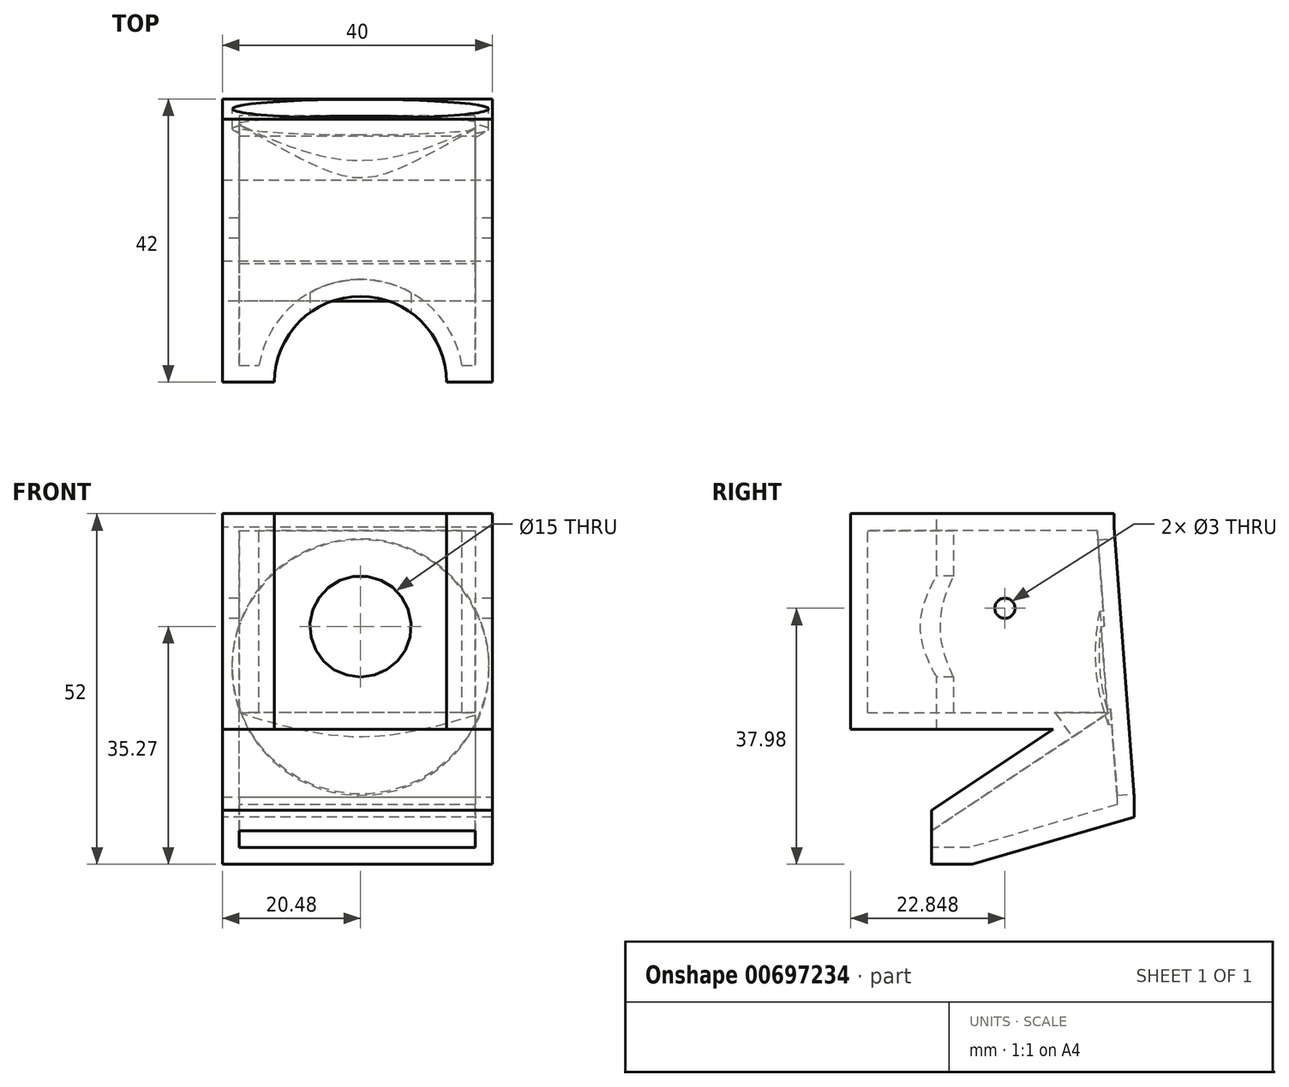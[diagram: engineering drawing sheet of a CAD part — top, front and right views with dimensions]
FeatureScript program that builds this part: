
annotation { "Feature Type Name" : "Feature", "Feature Type Description" : "" }
export const myFeature = defineFeature(function(context is Context, id is Id, definition is map)
    precondition{}
    {
        {
            var Q0;
            Q0=qCreatedBy(makeId("Top.planeOp"),FACE);
            var sketch = newSketch(context, id + "F0", { "sketchPlane" : qUnion([Q0])});
            skLineSegment(sketch, "E0.bottom", {"start": v(-20.48, 30.45) * mm, "end": v(19.52, 30.45) * mm});
            skLineSegment(sketch, "E0.top", {"start": v(-20.48, 0.45) * mm, "end": v(19.52, 0.45) * mm});
            skLineSegment(sketch, "E0.left", {"start": v(-20.48, 30.45) * mm, "end": v(-20.48, 0.45) * mm});
            skLineSegment(sketch, "E0.right", {"start": v(19.52, 30.45) * mm, "end": v(19.52, 0.45) * mm});
            skSolve(sketch);
        }
        {
            var Q0;
            Q0=makeQuery(id+"F0.imprint","IMPRINT",FACE,{"disambiguationData":[TD([[makeQuery(id+"F0.imprint","IMPRINT",EDGE,{"derivedFrom":sQuery(id+"F0.wireOp",EDGE,"E0.bottom")}),-1.0]])]});
            extrude(context, id + "F1", {"entities" : qUnion([Q0]), "depth" : 20 * mm, "offsetDistance" : 25 * mm});
        }
        {
            var Q0;
            Q0=makeQuery(id+"F1.opExtrude","CAP_EDGE",EDGE,{"disambiguationData":[OSD([sQuery(id+"F0.wireOp",EDGE,"E0.top")])],"isStart":false});
            chamfer(context, id + "F2", {"entities" : qUnion([Q0]), "chamferType" : ChamferType.TWO_OFFSETS, "width1" : 18 * mm, "oppositeDirection" : false, "width2" : 12 * mm, "tangentPropagation" : true});
        }
        {
            var Q0;
            Q0=makeQuery(id+"F1.opExtrude","CAP_EDGE",EDGE,{"disambiguationData":[OSD([sQuery(id+"F0.wireOp",EDGE,"E0.bottom")])],"isStart":true});
            chamfer(context, id + "F3", {"entities" : qUnion([Q0]), "chamferType" : ChamferType.TWO_OFFSETS, "width1" : 24 * mm, "oppositeDirection" : false, "width2" : 7 * mm, "tangentPropagation" : true});
        }
        {
            var Q0;
            Q0=makeQuery(id+"F1.opExtrude","CAP_FACE",FACE,{"disambiguationData":[OSD([sQuery(id+"F0.wireOp",EDGE,"E0.bottom"),sQuery(id+"F0.wireOp",EDGE,"E0.top"),sQuery(id+"F0.wireOp",EDGE,"E0.left"),sQuery(id+"F0.wireOp",EDGE,"E0.right")])],"isStart":false});
            extrude(context, id + "F4", {"entities" : qUnion([Q0]), "operationType" : NewBodyOperationType.ADD, "depth" : 30 * mm, "offsetDistance" : 25 * mm});
        }
        {
            var Q0;
            Q0=makeQuery(id+"F4.opExtrude","CAP_EDGE",EDGE,{"disambiguationData":[OSD([sQuery(id+"F0.wireOp",EDGE,"E0.bottom")])],"isStart":false});
            chamfer(context, id + "F5", {"entities" : qUnion([Q0]), "chamferType" : ChamferType.TWO_OFFSETS, "width1" : 40 * mm, "oppositeDirection" : false, "width2" : 3 * mm, "tangentPropagation" : true});
        }
        {
            var Q0;
            Q0=makeQuery(id+"F4.opExtrude","CAP_FACE",FACE,{"disambiguationData":[OSD([sQuery(id+"F0.wireOp",EDGE,"E0.bottom"),sQuery(id+"F0.wireOp",EDGE,"E0.top"),sQuery(id+"F0.wireOp",EDGE,"E0.left"),sQuery(id+"F0.wireOp",EDGE,"E0.right")])],"isStart":false});
            extrude(context, id + "F6", {"entities" : qUnion([Q0]), "operationType" : NewBodyOperationType.ADD, "depth" : 2 * mm, "offsetDistance" : 25 * mm});
        }
        {
            var Q0;
            {var subQ0=sQuery(id+"F0.wireOp",EDGE,"E0.right");var subQ1=sQuery(id+"F0.wireOp",EDGE,"E0.left");var subQ2=sQuery(id+"F0.wireOp",EDGE,"E0.top");var subQ3=sQuery(id+"F0.wireOp",EDGE,"E0.bottom");var subQ4=makeQuery(id+"F2.opChamfer","BLEND_EDGE",EDGE,{"blendedFrom":[makeQuery(id+"F1.opExtrude","CAP_EDGE",EDGE,{"disambiguationData":[OSD([subQ2])],"isStart":false}),makeQuery(id+"F1.opExtrude","CAP_FACE",FACE,{"disambiguationData":[OSD([subQ3,subQ2,subQ1,subQ0])],"isStart":false})],"blendedInto":[makeQuery(id+"F1.opExtrude","CAP_FACE",FACE,{"disambiguationData":[OSD([subQ3,subQ2,subQ1,subQ0])],"isStart":false})]});Q0=makeQuery(id+"F6.boolean.opBoolean","MERGE",FACE,{"derivedFrom":[makeQuery(id+"F4.opExtrude","SWEPT_FACE",FACE,{"disambiguationData":[OSD([subQ3,subQ2,subQ1,subQ0]),TDD([subQ4])]}),makeQuery(id+"F6.opExtrude","SWEPT_FACE",FACE,{"disambiguationData":[OSD([subQ3,subQ2,subQ1,subQ0]),TDD([makeQuery(id+"F4.opExtrude","CAP_EDGE",EDGE,{"disambiguationData":[OSD([subQ3,subQ2,subQ1,subQ0]),TDD([subQ4])],"isStart":false})])]})]});}
            extrude(context, id + "F7", {"entities" : qUnion([Q0]), "operationType" : NewBodyOperationType.ADD, "depth" : 30 * mm, "offsetDistance" : 25 * mm});
        }
        {
            var Q0;
            {var subQ0=sQuery(id+"F0.wireOp",EDGE,"E0.right");var subQ1=sQuery(id+"F0.wireOp",EDGE,"E0.left");var subQ2=sQuery(id+"F0.wireOp",EDGE,"E0.top");var subQ3=sQuery(id+"F0.wireOp",EDGE,"E0.bottom");var subQ4=makeQuery(id+"F1.opExtrude","CAP_FACE",FACE,{"disambiguationData":[OSD([subQ3,subQ2,subQ1,subQ0])],"isStart":false});var subQ5=subQ4;var subQ6=makeQuery(id+"F2.opChamfer","BLEND_FACE",FACE,{"disambiguationData":[OSD([subQ2])]});var subQ7=subQ6;Q0=makeQuery(id+"FwOc9T6z4XyDqVD_1.boolean.opBoolean","MERGE",FACE,{"derivedFrom":[makeQuery(id+"FGftwgvc4cN77NT_1.boolean.opBoolean","MERGE",FACE,{"derivedFrom":[makeQuery(id+"F7.boolean.opBoolean","MERGE",FACE,{"derivedFrom":[makeQuery(id+"F6.opExtrude","CAP_FACE",FACE,{"disambiguationData":[OSD([subQ3,subQ2,subQ1,subQ0])],"isStart":false}),makeQuery(id+"F7.opExtrude","SWEPT_FACE",FACE,{"disambiguationData":[OSD([subQ3,subQ2,subQ1,subQ0]),TDD([makeQuery(id+"F6.opExtrude","CAP_EDGE",EDGE,{"disambiguationData":[OSD([subQ3,subQ2,subQ1,subQ0]),TDD([makeQuery(id+"F4.opExtrude","CAP_EDGE",EDGE,{"disambiguationData":[OSD([subQ3,subQ2,subQ1,subQ0]),TDD([makeQuery(id+"F2.opChamfer","BLEND_EDGE",EDGE,{"blendedFrom":[makeQuery(id+"F1.opExtrude","CAP_EDGE",EDGE,{"disambiguationData":[OSD([subQ2])],"isStart":false}),subQ4],"blendedInto":[subQ4]})])],"isStart":false})])],"isStart":false})])]})]}),makeQuery(id+"FGftwgvc4cN77NT_1.opExtrude","SWEPT_FACE",FACE,{"disambiguationData":[OSD([subQ3,subQ2,subQ1,subQ0]),TDD([makeQuery(id+"F7.opExtrude","SWEPT_EDGE",EDGE,{"disambiguationData":[OSD([subQ3,subQ2,subQ1,subQ0]),TDD([makeQuery(id+"F6.opExtrude","CAP_VERTEX",VERTEX,{"disambiguationData":[OSD([subQ3,subQ2,subQ1,subQ0]),TDD([makeQuery(id+"F4.opExtrude","CAP_VERTEX",VERTEX,{"disambiguationData":[OSD([subQ3,subQ2,subQ1,subQ0]),TDD([makeQuery(id+"Fd9LKxhcyNDBXAF_1.opFillet","BLEND_VERTEX",VERTEX,{"blendedFrom":[makeQuery(id+"FYLmRwXSOBME0PA_1.opChamfer","BLEND_EDGE",EDGE,{"blendedFrom":[makeQuery(id+"F1.opExtrude","SWEPT_EDGE",EDGE,{"disambiguationData":[OSD([subQ2,subQ1])]}),subQ6],"blendedInto":[subQ6]}),subQ7,subQ5],"blendedInto":[subQ7,subQ5]})])],"isStart":false})])],"isStart":false})])]})])]})]}),makeQuery(id+"FwOc9T6z4XyDqVD_1.opExtrude","SWEPT_FACE",FACE,{"disambiguationData":[OSD([subQ3,subQ2,subQ1,subQ0]),TDD([makeQuery(id+"F7.opExtrude","SWEPT_EDGE",EDGE,{"disambiguationData":[OSD([subQ3,subQ2,subQ1,subQ0]),TDD([makeQuery(id+"F6.opExtrude","CAP_VERTEX",VERTEX,{"disambiguationData":[OSD([subQ3,subQ2,subQ1,subQ0]),TDD([makeQuery(id+"F4.opExtrude","CAP_VERTEX",VERTEX,{"disambiguationData":[OSD([subQ3,subQ2,subQ1,subQ0]),TDD([makeQuery(id+"Fd9LKxhcyNDBXAF_1.opFillet","BLEND_VERTEX",VERTEX,{"blendedFrom":[makeQuery(id+"FYLmRwXSOBME0PA_1.opChamfer","BLEND_EDGE",EDGE,{"blendedFrom":[makeQuery(id+"F1.opExtrude","SWEPT_EDGE",EDGE,{"disambiguationData":[OSD([subQ2,subQ0])]}),subQ6],"blendedInto":[subQ6]}),subQ7,subQ5],"blendedInto":[subQ7,subQ5]})])],"isStart":false})])],"isStart":false})])]})])]})]});}
            var sketch = newSketch(context, id + "F8", { "sketchPlane" : qUnion([Q0])});
            skCircle(sketch, "E1", {"center": v(0, -11.55) * mm, "radius": 3.46 * mm});
            skSolve(sketch);
        }
        {
            var Q0;
            Q0=sQuery(id+"F8.wireOp",VERTEX,"E1.center");
            var Q1;
            Q1=makeQuery(id+"F1.opExtrude","SWEPT_BODY",BODY,{"disambiguationData":[OSD([sQuery(id+"F0.wireOp",EDGE,"E0.bottom"),sQuery(id+"F0.wireOp",EDGE,"E0.top"),sQuery(id+"F0.wireOp",EDGE,"E0.left"),sQuery(id+"F0.wireOp",EDGE,"E0.right")])]});
            hole(context, id + "F9", {"style" : HoleStyle.SIMPLE, "endStyle" : HoleEndStyle.BLIND, "holeDiameter" : 25.5 * mm, "majorDiameter" : 5 * mm, "holeDepth" : 40 * mm, "isTappedThrough" : true, "tappedDepth" : 12 * mm, "tapClearance" : 3, "locations" : qUnion([Q0]), "scope" : qUnion([Q1])});
        }
        {
            var Q0;
            Q0=makeQuery(id+"F5.opChamfer","BLEND_FACE",FACE,{"disambiguationData":[OSD([sQuery(id+"F0.wireOp",EDGE,"E0.bottom")])]});
            var sketch = newSketch(context, id + "F10", { "sketchPlane" : qUnion([Q0])});
            skLineSegment(sketch, "E2.bottom", {"start": v(20.48, 47.8) * mm, "end": v(-19.52, 47.8) * mm});
            skLineSegment(sketch, "E2.top", {"start": v(20.48, 7.7) * mm, "end": v(-19.52, 7.7) * mm});
            skLineSegment(sketch, "E2.left", {"start": v(20.48, 47.8) * mm, "end": v(20.48, 7.7) * mm});
            skLineSegment(sketch, "E2.right", {"start": v(-19.52, 47.8) * mm, "end": v(-19.52, 7.7) * mm});
            skSolve(sketch);
        }
        {
            var Q0;
            Q0=makeQuery(id+"F10.imprint","IMPRINT",FACE,{"disambiguationData":[TD([[makeQuery(id+"F10.imprint","IMPRINT",EDGE,{"derivedFrom":sQuery(id+"F10.wireOp",EDGE,"E2.bottom")}),-1.0]])]});
            var sketch = newSketch(context, id + "F11", { "sketchPlane" : qUnion([Q0])});
            skCircle(sketch, "E3", {"center": v(0, 27.12) * mm, "radius": 18.85 * mm});
            skSolve(sketch);
        }
        {
            var Q0;
            Q0=makeQuery(id+"F1.opExtrude","SWEPT_FACE",FACE,{"disambiguationData":[OSD([sQuery(id+"F0.wireOp",EDGE,"E0.top")])]});
            shell(context, id + "F12", {"entities" : qUnion([Q0]), "thickness" : 2.5 * mm});
        }
        {
            var Q0;
            Q0=sQuery(id+"F11.wireOp",VERTEX,"E3.center");
            var Q1;
            Q1=makeQuery(id+"F1.opExtrude","SWEPT_BODY",BODY,{"disambiguationData":[OSD([sQuery(id+"F0.wireOp",EDGE,"E0.bottom"),sQuery(id+"F0.wireOp",EDGE,"E0.top"),sQuery(id+"F0.wireOp",EDGE,"E0.left"),sQuery(id+"F0.wireOp",EDGE,"E0.right")])]});
            hole(context, id + "F13", {"style" : HoleStyle.SIMPLE, "endStyle" : HoleEndStyle.BLIND, "holeDiameter" : 38 * mm, "majorDiameter" : 5 * mm, "holeDepth" : 3 * mm, "isTappedThrough" : true, "tappedDepth" : 12 * mm, "tapClearance" : 3, "locations" : qUnion([Q0]), "scope" : qUnion([Q1])});
        }
        {
            var Q0;
            {var subQ0=sQuery(id+"F0.wireOp",EDGE,"E0.right");var subQ1=sQuery(id+"F0.wireOp",EDGE,"E0.left");var subQ2=sQuery(id+"F0.wireOp",EDGE,"E0.top");var subQ3=sQuery(id+"F0.wireOp",EDGE,"E0.bottom");var subQ4=makeQuery(id+"F1.opExtrude","SWEPT_FACE",FACE,{"disambiguationData":[OSD([subQ1])]});Q0=makeQuery(id+"F9.hole-0.boolean.opBoolean","SPLIT",FACE,{"disambiguationData":[TD([subQ4])],"derivedFrom":makeQuery(id+"F7.opExtrude","CAP_FACE",FACE,{"disambiguationData":[OSD([subQ3,subQ2,subQ1,subQ0])],"isStart":false})});}
            var sketch = newSketch(context, id + "F14", { "sketchPlane" : qUnion([Q0])});
            skCircle(sketch, "E4", {"center": v(0, 35.27) * mm, "radius": 5.09 * mm});
            skSolve(sketch);
        }
        {
            var Q0;
            Q0=sQuery(id+"F14.wireOp",VERTEX,"E4.center");
            var Q1;
            Q1=makeQuery(id+"F1.opExtrude","SWEPT_BODY",BODY,{"disambiguationData":[OSD([sQuery(id+"F0.wireOp",EDGE,"E0.bottom"),sQuery(id+"F0.wireOp",EDGE,"E0.top"),sQuery(id+"F0.wireOp",EDGE,"E0.left"),sQuery(id+"F0.wireOp",EDGE,"E0.right")])]});
            hole(context, id + "F15", {"style" : HoleStyle.SIMPLE, "endStyle" : HoleEndStyle.BLIND, "holeDiameter" : 15 * mm, "majorDiameter" : 5 * mm, "holeDepth" : 15 * mm, "isTappedThrough" : true, "tappedDepth" : 12 * mm, "tapClearance" : 3, "locations" : qUnion([Q0]), "scope" : qUnion([Q1])});
        }
        {
            var Q0;
            {var subQ0=sQuery(id+"F0.wireOp",EDGE,"E0.left");var subQ1=makeQuery(id+"F1.opExtrude","SWEPT_FACE",FACE,{"disambiguationData":[OSD([subQ0])]});var subQ2=sQuery(id+"F0.wireOp",EDGE,"E0.right");var subQ3=sQuery(id+"F0.wireOp",EDGE,"E0.top");var subQ4=sQuery(id+"F0.wireOp",EDGE,"E0.bottom");var subQ5=makeQuery(id+"F2.opChamfer","BLEND_VERTEX",VERTEX,{"blendedFrom":[makeQuery(id+"F1.opExtrude","CAP_EDGE",EDGE,{"disambiguationData":[OSD([subQ3])],"isStart":false}),makeQuery(id+"F1.opExtrude","CAP_FACE",FACE,{"disambiguationData":[OSD([subQ4,subQ3,subQ0,subQ2])],"isStart":false}),subQ1],"blendedInto":[makeQuery(id+"F1.opExtrude","CAP_FACE",FACE,{"disambiguationData":[OSD([subQ4,subQ3,subQ0,subQ2])],"isStart":false}),subQ1]});Q0=makeQuery(id+"F7.boolean.opBoolean","MERGE",FACE,{"derivedFrom":[makeQuery(id+"F6.boolean.opBoolean","MERGE",FACE,{"derivedFrom":[makeQuery(id+"F4.boolean.opBoolean","MERGE",FACE,{"derivedFrom":[subQ1,makeQuery(id+"F4.opExtrude","SWEPT_FACE",FACE,{"disambiguationData":[OSD([subQ0])]})]}),makeQuery(id+"F6.opExtrude","SWEPT_FACE",FACE,{"disambiguationData":[OSD([subQ0])]})]}),makeQuery(id+"F7.opExtrude","SWEPT_FACE",FACE,{"disambiguationData":[OSD([subQ4,subQ3,subQ0,subQ2]),TDD([makeQuery(id+"F6.boolean.opBoolean","MERGE",EDGE,{"derivedFrom":[makeQuery(id+"F4.opExtrude","SWEPT_EDGE",EDGE,{"disambiguationData":[OSD([subQ4,subQ3,subQ0,subQ2]),TDD([subQ5])]}),makeQuery(id+"F6.opExtrude","SWEPT_EDGE",EDGE,{"disambiguationData":[OSD([subQ4,subQ3,subQ0,subQ2]),TDD([makeQuery(id+"F4.opExtrude","CAP_VERTEX",VERTEX,{"disambiguationData":[OSD([subQ4,subQ3,subQ0,subQ2]),TDD([subQ5])],"isStart":false})])]})]})])]})]});}
            var sketch = newSketch(context, id + "F16", { "sketchPlane" : qUnion([Q0])});
            skCircle(sketch, "E5", {"center": v(-11.3, 37.98) * mm, "radius": 3.75 * mm});
            skSolve(sketch);
        }
        {
            var Q0;
            Q0=sQuery(id+"F16.wireOp",VERTEX,"E5.center");
            var Q1;
            Q1=makeQuery(id+"F1.opExtrude","SWEPT_BODY",BODY,{"disambiguationData":[OSD([sQuery(id+"F0.wireOp",EDGE,"E0.bottom"),sQuery(id+"F0.wireOp",EDGE,"E0.top"),sQuery(id+"F0.wireOp",EDGE,"E0.left"),sQuery(id+"F0.wireOp",EDGE,"E0.right")])]});
            hole(context, id + "F17", {"style" : HoleStyle.SIMPLE, "endStyle" : HoleEndStyle.THROUGH, "holeDiameter" : 3 * mm, "majorDiameter" : 5 * mm, "isTappedThrough" : true, "tappedDepth" : 12 * mm, "tapClearance" : 3, "locations" : qUnion([Q0]), "scope" : qUnion([Q1])});
        }
    });
